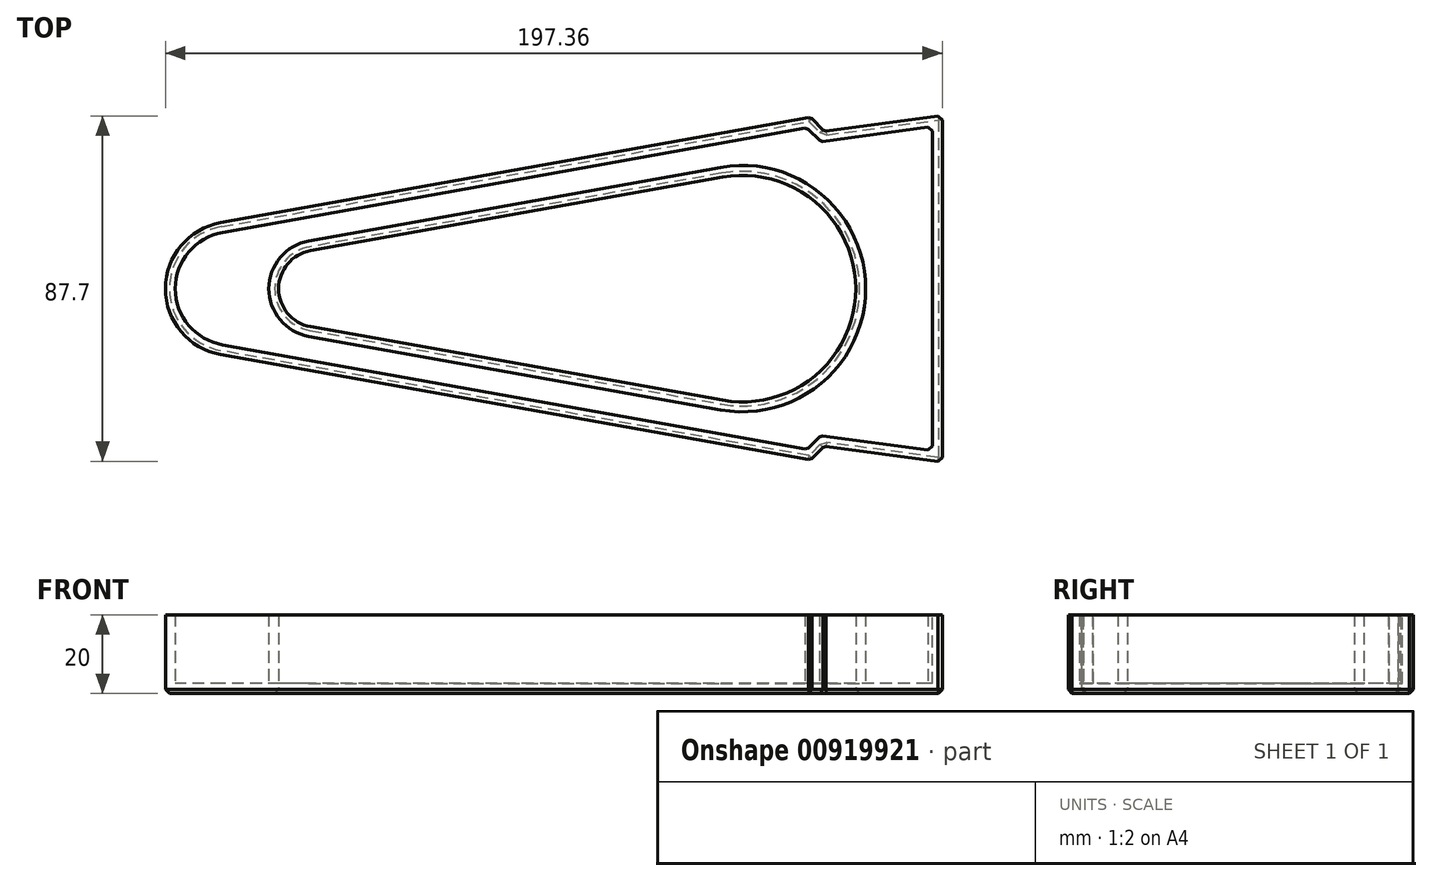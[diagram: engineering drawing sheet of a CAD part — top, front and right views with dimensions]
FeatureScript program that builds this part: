
annotation { "Feature Type Name" : "Feature", "Feature Type Description" : "" }
export const myFeature = defineFeature(function(context is Context, id is Id, definition is map)
    precondition{}
    {
        {
            var Q0;
            Q0=qCreatedBy(makeId("Top.planeOp"),FACE);
            var sketch = newSketch(context, id + "F0", { "sketchPlane" : qUnion([Q0])});
            skCircle(sketch, "E0", {"center": v(50, 0) * mm, "radius": 28.8 * mm});
            skCircle(sketch, "E1", {"center": v(-58, 0) * mm, "radius": 9.8 * mm});
            skLineSegment(sketch, "E2", {"start": v(-59.72, 9.65) * mm, "end": v(44.93, 28.35) * mm});
            skLineSegment(sketch, "E3", {"start": v(-59.72, -9.65) * mm, "end": v(44.93, -28.35) * mm});
            skLineSegment(sketch, "E4", {"start": v(100.8, 44) * mm, "end": v(100.8, -44) * mm});
            skLineSegment(sketch, "E5", {"start": v(100.8, 44) * mm, "end": v(70.8, 40) * mm});
            skLineSegment(sketch, "E6", {"start": v(70.8, 40) * mm, "end": v(67.3, 43.52) * mm});
            skLineSegment(sketch, "E7", {"start": v(67.3, 43.52) * mm, "end": v(-82.54, 16.74) * mm});
            skLineSegment(sketch, "E8", {"start": v(100.8, -44) * mm, "end": v(70.8, -40) * mm});
            skLineSegment(sketch, "E9", {"start": v(70.8, -40) * mm, "end": v(67.3, -43.52) * mm});
            skLineSegment(sketch, "E10", {"start": v(67.3, -43.52) * mm, "end": v(-82.54, -16.74) * mm});
            skLineSegment(sketch, "E11", {"start": v(70.8, 40) * mm, "end": v(70.8, -40) * mm, "construction": true});
            skCircle(sketch, "E12", {"center": v(-79.55, 0) * mm, "radius": 17 * mm});
            skSolve(sketch);
        }
        {
            var Q0;
            Q0=makeQuery(id+"F0.imprint","IMPRINT",FACE,{"disambiguationData":[TD([[makeQuery(id+"F0.imprint","IMPRINT",EDGE,{"derivedFrom":sQuery(id+"F0.wireOp",EDGE,"E4")}),-1.0]])]});
            var Q1;
            {var subQ2=sQuery(id+"F0.wireOp",EDGE,"E2");var subQ4=sQuery(id+"F0.wireOp",EDGE,"E1");var subQ5=makeQuery(id+"F0.imprint","INTERSECT",VERTEX,{"derivedFrom":[subQ4,subQ2]});Q1=makeQuery(id+"F0.imprint","IMPRINT",FACE,{"disambiguationData":[TD([[makeQuery(id+"F0.imprint","IMPRINT",EDGE,{"disambiguationData":[TD([[subQ5,-1.0]])],"derivedFrom":subQ4}),-1.0]])]});}
            var Q2;
            {var subQ0=sQuery(id+"F0.wireOp",EDGE,"E12");var subQ1=makeQuery(id+"F0.imprint","INTERSECT",VERTEX,{"derivedFrom":[sQuery(id+"F0.wireOp",EDGE,"E7"),subQ0]});Q2=makeQuery(id+"F0.imprint","IMPRINT",FACE,{"disambiguationData":[TD([[makeQuery(id+"F0.imprint","IMPRINT",EDGE,{"disambiguationData":[TD([[subQ1,-1.0]])],"derivedFrom":subQ0}),1.0]])]});}
            extrude(context, id + "F1", {"entities" : qUnion([Q0, Q1, Q2]), "depth" : 20 * mm, "offsetDistance" : 25 * mm});
        }
        {
            var Q0;
            Q0=makeQuery(id+"F1.opExtrude","CAP_FACE",FACE,{"disambiguationData":[OSD([sQuery(id+"F0.wireOp",EDGE,"E0"),sQuery(id+"F0.wireOp",EDGE,"E1"),sQuery(id+"F0.wireOp",EDGE,"E2"),sQuery(id+"F0.wireOp",EDGE,"E3"),sQuery(id+"F0.wireOp",EDGE,"E4"),sQuery(id+"F0.wireOp",EDGE,"E5"),sQuery(id+"F0.wireOp",EDGE,"E6"),sQuery(id+"F0.wireOp",EDGE,"E7"),sQuery(id+"F0.wireOp",EDGE,"E8"),sQuery(id+"F0.wireOp",EDGE,"E9"),sQuery(id+"F0.wireOp",EDGE,"E10"),sQuery(id+"F0.wireOp",EDGE,"Dk3eekXj-WzE7-mZ2Z-h0g7-VJLs4lcgVmIX")])],"isStart":false});
            shell(context, id + "F2", {"entities" : qUnion([Q0]), "thickness" : 2.5 * mm});
        }
        {
            var Q0;
            Q0=makeQuery(id+"F1.opExtrude","SWEPT_EDGE",EDGE,{"disambiguationData":[OSD([sQuery(id+"F0.wireOp",EDGE,"E4"),sQuery(id+"F0.wireOp",EDGE,"E8")])]});
            var Q1;
            Q1=makeQuery(id+"F1.opExtrude","SWEPT_EDGE",EDGE,{"disambiguationData":[OSD([sQuery(id+"F0.wireOp",EDGE,"E4"),sQuery(id+"F0.wireOp",EDGE,"E5")])]});
            var Q2;
            Q2=makeQuery(id+"F2.opShell","OFFSET_EDGE",EDGE,{"disambiguationData":[OSD([sQuery(id+"F0.wireOp",EDGE,"E4"),sQuery(id+"F0.wireOp",EDGE,"E5")])]});
            var Q3;
            Q3=makeQuery(id+"F2.opShell","OFFSET_EDGE",EDGE,{"disambiguationData":[OSD([sQuery(id+"F0.wireOp",EDGE,"E4"),sQuery(id+"F0.wireOp",EDGE,"E8")])]});
            var Q4;
            Q4=makeQuery(id+"F1.opExtrude","CAP_EDGE",EDGE,{"disambiguationData":[OSD([sQuery(id+"F0.wireOp",EDGE,"E3")])],"isStart":true});
            var Q5;
            Q5=makeQuery(id+"F1.opExtrude","SWEPT_EDGE",EDGE,{"disambiguationData":[OSD([sQuery(id+"F0.wireOp",EDGE,"E9"),sQuery(id+"F0.wireOp",EDGE,"E10")])]});
            var Q6;
            Q6=makeQuery(id+"F1.opExtrude","SWEPT_EDGE",EDGE,{"disambiguationData":[OSD([sQuery(id+"F0.wireOp",EDGE,"E8"),sQuery(id+"F0.wireOp",EDGE,"E9")])]});
            var Q7;
            Q7=makeQuery(id+"F1.opExtrude","SWEPT_EDGE",EDGE,{"disambiguationData":[OSD([sQuery(id+"F0.wireOp",EDGE,"E6"),sQuery(id+"F0.wireOp",EDGE,"E7")])]});
            var Q8;
            Q8=makeQuery(id+"F1.opExtrude","SWEPT_EDGE",EDGE,{"disambiguationData":[OSD([sQuery(id+"F0.wireOp",EDGE,"E5"),sQuery(id+"F0.wireOp",EDGE,"E6")])]});
            var Q9;
            Q9=makeQuery(id+"F2.opShell","OFFSET_EDGE",EDGE,{"disambiguationData":[OSD([sQuery(id+"F0.wireOp",EDGE,"E6"),sQuery(id+"F0.wireOp",EDGE,"E7")])]});
            var Q10;
            Q10=makeQuery(id+"F2.opShell","OFFSET_EDGE",EDGE,{"disambiguationData":[OSD([sQuery(id+"F0.wireOp",EDGE,"E5"),sQuery(id+"F0.wireOp",EDGE,"E6")])]});
            var Q11;
            Q11=makeQuery(id+"F2.opShell","OFFSET_EDGE",EDGE,{"disambiguationData":[OSD([sQuery(id+"F0.wireOp",EDGE,"E8"),sQuery(id+"F0.wireOp",EDGE,"E9")])]});
            var Q12;
            Q12=makeQuery(id+"F2.opShell","OFFSET_EDGE",EDGE,{"disambiguationData":[OSD([sQuery(id+"F0.wireOp",EDGE,"E9"),sQuery(id+"F0.wireOp",EDGE,"E10")])]});
            var Q13;
            Q13=makeQuery(id+"F1.opExtrude","CAP_EDGE",EDGE,{"disambiguationData":[OSD([sQuery(id+"F0.wireOp",EDGE,"E10")])],"isStart":true});
            var Q14;
            Q14=makeQuery(id+"F1.opExtrude","CAP_EDGE",EDGE,{"disambiguationData":[OSD([sQuery(id+"F0.wireOp",EDGE,"E9")])],"isStart":true});
            var Q15;
            Q15=makeQuery(id+"F1.opExtrude","CAP_EDGE",EDGE,{"disambiguationData":[OSD([sQuery(id+"F0.wireOp",EDGE,"E4")])],"isStart":true});
            var Q16;
            Q16=makeQuery(id+"F1.opExtrude","CAP_EDGE",EDGE,{"disambiguationData":[OSD([sQuery(id+"F0.wireOp",EDGE,"E6")])],"isStart":true});
            chamfer(context, id + "F3", {"entities" : qUnion([Q0, Q1, Q2, Q3, Q4, Q5, Q6, Q7, Q8, Q9, Q10, Q11, Q12, Q13, Q14, Q15, Q16]), "width" : 1 * mm, "tangentPropagation" : true});
        }
    });
